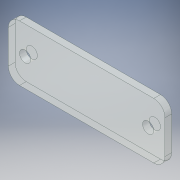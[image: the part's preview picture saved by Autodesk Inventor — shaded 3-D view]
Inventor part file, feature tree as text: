
AUTODESK INVENTOR PART (.ipt)
format: ipt  version: 2019 (Build 230136000, 136)  size: 114,688 bytes
history: native  units: in
note: dims shown in document units (in); Inventor stores cm internally (conversion verified against a paired STEP export)
features: fillet x4, extrude x2, sketch x2
ambient origin geometry x8: Origin, YZ Plane, XZ Plane, XY Plane, X Axis, Y Axis, Z Axis, Center Point
bodies: Solid1 (feature_tree)
feature tree (8):
  extrude  "Extrusion1"  Depth=2.7559in
  fillet  "Fillet1"  Radius=0.1181in
  fillet  "Fillet2"  Radius=0.1969in
  fillet  "Fillet3"  Radius=0.1969in
  fillet  "Fillet4"  Radius=0.1969in
  extrude  "Extrusion2"  TaperAngle=0.0deg  [1 undecoded]
  sketch  "Sketch1"  dims[d0=0.9843in d1=2.7559in d2=0.1181in d3=0.0in d4=0.1969in d5=0.1969in d6=0.1969in]
  sketch  "Sketch2"  dims[d7=0.1969in d14=0.0in d15=0.0in]
note: 1 required parameter value undecoded (feature->parameter linkage not recoverable at this tier; creation-order binding heuristic only, values carry confidence <= 0.55)
